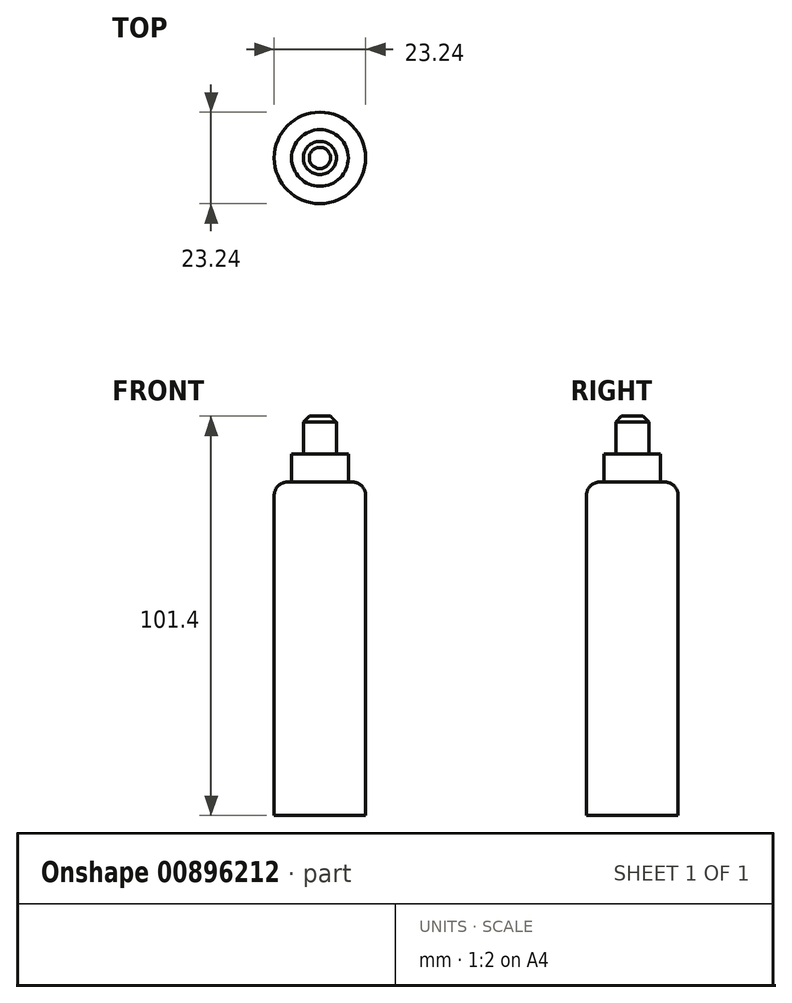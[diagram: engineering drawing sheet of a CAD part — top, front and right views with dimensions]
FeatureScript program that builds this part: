
annotation { "Feature Type Name" : "Feature", "Feature Type Description" : "" }
export const myFeature = defineFeature(function(context is Context, id is Id, definition is map)
    precondition{}
    {
        {
            var Q0;
            Q0=qCreatedBy(makeId("Top.planeOp"),FACE);
            var sketch = newSketch(context, id + "F0", { "sketchPlane" : qUnion([Q0])});
            skCircle(sketch, "E0", {"center": v(0, 0) * mm, "radius": 11.62 * mm});
            skSolve(sketch);
        }
        {
            var Q0;
            Q0=makeQuery(id+"F0.imprint","IMPRINT",FACE,{"disambiguationData":[TD([[makeQuery(id+"F0.imprint","IMPRINT",EDGE,{"derivedFrom":sQuery(id+"F0.wireOp",EDGE,"E0")}),1.0]])]});
            extrude(context, id + "F1", {"entities" : qUnion([Q0]), "depth" : 84.7 * mm, "offsetDistance" : 25 * mm});
        }
        {
            var Q0;
            Q0=makeQuery(id+"F1.opExtrude","CAP_FACE",FACE,{"disambiguationData":[OSD([sQuery(id+"F0.wireOp",EDGE,"E0")])],"isStart":false});
            var sketch = newSketch(context, id + "F2", { "sketchPlane" : qUnion([Q0])});
            skCircle(sketch, "E1", {"center": v(0, 0) * mm, "radius": 7.2 * mm});
            skSolve(sketch);
        }
        {
            var Q0;
            Q0=makeQuery(id+"F2.imprint","IMPRINT",FACE,{"disambiguationData":[TD([[makeQuery(id+"F2.imprint","IMPRINT",EDGE,{"derivedFrom":sQuery(id+"F2.wireOp",EDGE,"E1")}),1.0]])]});
            extrude(context, id + "F3", {"entities" : qUnion([Q0]), "operationType" : NewBodyOperationType.ADD, "depth" : 7.1 * mm, "offsetDistance" : 25 * mm});
        }
        {
            var Q0;
            Q0=makeQuery(id+"F3.opExtrude","CAP_FACE",FACE,{"disambiguationData":[OSD([sQuery(id+"F2.wireOp",EDGE,"E1")])],"isStart":false});
            var sketch = newSketch(context, id + "F4", { "sketchPlane" : qUnion([Q0])});
            skCircle(sketch, "E2", {"center": v(0, 0) * mm, "radius": 4.2 * mm});
            skSolve(sketch);
        }
        {
            var Q0;
            Q0=makeQuery(id+"F4.imprint","IMPRINT",FACE,{"disambiguationData":[TD([[makeQuery(id+"F4.imprint","IMPRINT",EDGE,{"derivedFrom":sQuery(id+"F4.wireOp",EDGE,"E2")}),1.0]])]});
            extrude(context, id + "F5", {"entities" : qUnion([Q0]), "operationType" : NewBodyOperationType.ADD, "depth" : 9.6 * mm, "offsetDistance" : 25 * mm});
        }
        {
            var Q0;
            Q0=makeQuery(id+"F1.opExtrude","CAP_EDGE",EDGE,{"disambiguationData":[OSD([sQuery(id+"F0.wireOp",EDGE,"E0")])],"isStart":false});
            fillet(context, id + "F6", {"entities" : qUnion([Q0]), "radius" : 3.38 * mm, "tangentPropagation" : true, "allowEdgeOverflow" : false});
        }
        {
            var Q0;
            Q0=makeQuery(id+"F5.opExtrude","CAP_EDGE",EDGE,{"disambiguationData":[OSD([sQuery(id+"F4.wireOp",EDGE,"E2")])],"isStart":false});
            chamfer(context, id + "F7", {"entities" : qUnion([Q0]), "width" : 1.5 * mm, "tangentPropagation" : true});
        }
    });
